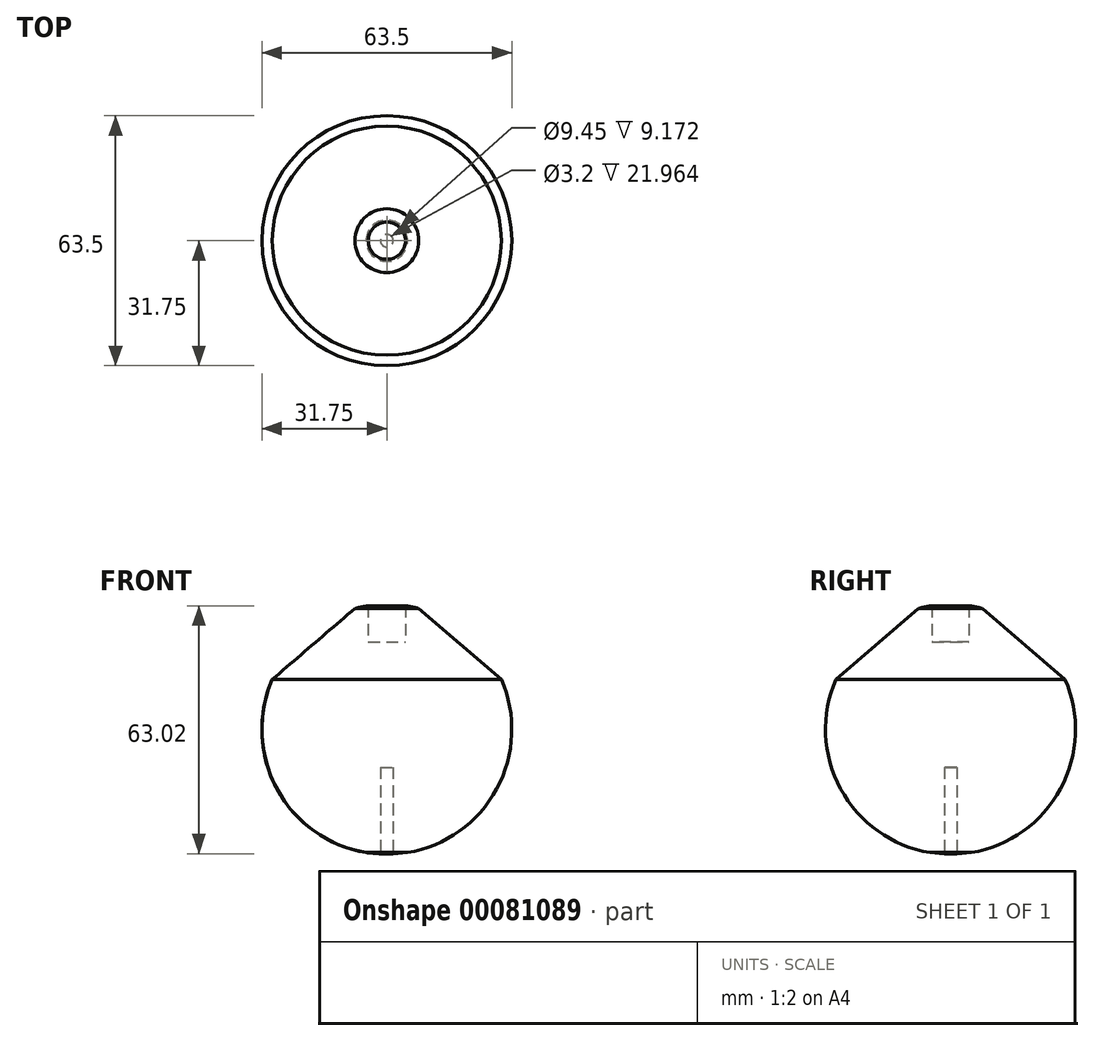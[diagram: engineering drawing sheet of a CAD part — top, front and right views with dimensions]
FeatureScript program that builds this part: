
annotation { "Feature Type Name" : "Feature", "Feature Type Description" : "" }
export const myFeature = defineFeature(function(context is Context, id is Id, definition is map)
    precondition{}
    {
        {
            var Q0;
            Q0=qCreatedBy(makeId("Front.planeOp"),FACE);
            var sketch = newSketch(context, id + "F0", { "sketchPlane" : qUnion([Q0])});
            skArc(sketch, "E0", {"start": v(-22.54, 16.5) * mm, "mid": v(-25.88, -10.52) * mm, "end": v(-4.63, -27.55) * mm});
            skLineSegment(sketch, "E1", {"start": v(0, 0) * mm, "end": v(0, 16.51) * mm});
            skLineSegment(sketch, "E2", {"start": v(0, 16.51) * mm, "end": v(-7.26, 16.51) * mm});
            skLineSegment(sketch, "E3", {"start": v(0, 0) * mm, "end": v(0, -27.94) * mm});
            skLineSegment(sketch, "E4", {"start": v(0, -27.94) * mm, "end": v(0, 35.56) * mm});
            skLineSegment(sketch, "E5", {"start": v(-4.72, 35.56) * mm, "end": v(-4.72, 16.51) * mm});
            skLineSegment(sketch, "E6", {"start": v(0, 35.56) * mm, "end": v(0, 26.03) * mm});
            skLineSegment(sketch, "E7", {"start": v(0, 26.03) * mm, "end": v(-4.72, 26.03) * mm});
            skLineSegment(sketch, "E8.trimOffspring", {"start": v(-7.26, 16.51) * mm, "end": v(22.54, 16.51) * mm});
            skLineSegment(sketch, "E9.trimOffspring", {"start": v(-19.3, 16.51) * mm, "end": v(-22.54, 16.51) * mm});
            skPoint(sketch, "E10", {"position": v(-7.26, -3.67) * mm});
            skPoint(sketch, "E11", {"position": v(-16.16, -5.93) * mm});
            skPoint(sketch, "E12", {"position": v(-24.25, -7.55) * mm});
            skLineSegment(sketch, "E13", {"start": v(-24.25, -7.55) * mm, "end": v(-24.25, -7.55) * mm});
            skPoint(sketch, "E14", {"position": v(-24.43, 6.97) * mm});
            skPoint(sketch, "E15.3.internal.snap0", {"position": v(7.64, 16.51) * mm});
            skLineSegment(sketch, "E16", {"start": v(-1.6, -27.8) * mm, "end": v(-13.82, -26.79) * mm});
            skLineSegment(sketch, "E17", {"start": v(0, -27.94) * mm, "end": v(0, -5.84) * mm});
            skLineSegment(sketch, "E18", {"start": v(0, -5.84) * mm, "end": v(-1.6, -5.84) * mm});
            skLineSegment(sketch, "E19", {"start": v(-1.6, -5.84) * mm, "end": v(-1.6, -27.8) * mm});
            skArc(sketch, "E20.trimOffspring", {"start": v(0, -27.94) * mm, "mid": v(24.92, -12.64) * mm, "end": v(22.54, 16.51) * mm});
            skArc(sketch, "E21.trimOffspring", {"start": v(0, -25.4) * mm, "mid": v(23.07, -10.63) * mm, "end": v(19.3, 16.51) * mm});
            skLineSegment(sketch, "E22", {"start": v(-22.54, 16.5) * mm, "end": v(-8.1, 34.5) * mm});
            skFitSpline(sketch, "E23.trimOffspring", {"points": [v(-24.43, 6.97) * mm, v(-7.26, 12.37) * mm, v(-9.1, 16.51) * mm], "startDerivative": vector(32.41, -14.69) * mm, "endDerivative": vector(-11.55, 14.27) * mm});
            skLineSegment(sketch, "E24", {"start": v(0, -27.94) * mm, "end": v(0, 3.8) * mm});
            skArc(sketch, "E25", {"start": v(-4.72, 35.2) * mm, "mid": v(-6.43, 34.9) * mm, "end": v(-8.1, 34.5) * mm});
            skLineSegment(sketch, "E26", {"start": v(-1.6, -27.8) * mm, "end": v(-1.6, -27.9) * mm});
            skArc(sketch, "E27.trimOffspring", {"start": v(0, -27.94) * mm, "mid": v(31.75, 3.8) * mm, "end": v(0, 35.56) * mm});
            skLineSegment(sketch, "E28", {"start": v(-22.54, 16.5) * mm, "end": v(-29.1, 16.5) * mm});
            skLineSegment(sketch, "E29", {"start": v(-29.1, 16.5) * mm, "end": v(-8.1, 34.5) * mm});
            skArc(sketch, "E30.trimOffspring", {"start": v(-29.1, 16.5) * mm, "mid": v(-27, -12.9) * mm, "end": v(-1.6, -27.9) * mm});
            skSolve(sketch);
        }
        {
            var Q0;
            {var subQ0=sQuery(id+"F0.wireOp",EDGE,"E13");var subQ1=sQuery(id+"F0.wireOp",EDGE,"tVGfZYd6-jjf8-WeDL-8lbz-A1Di6X17U0wS");var subQ2=makeQuery(id+"F0.imprint","INTERSECT",VERTEX,{"disambiguationData":[OD(0.0)],"derivedFrom":[subQ1,subQ0]});Q0=makeQuery(id+"F0.imprint","IMPRINT",FACE,{"disambiguationData":[TD([[makeQuery(id+"F0.imprint","IMPRINT",EDGE,{"disambiguationData":[TD([[subQ2,-1.0]])],"derivedFrom":subQ1}),1.0]])]});}
            var Q1;
            {var subQ0=sQuery(id+"F0.wireOp",EDGE,"tVGfZYd6-jjf8-WeDL-8lbz-A1Di6X17U0wS");var subQ1=sQuery(id+"F0.wireOp",EDGE,"bDiMBlMv-fEZ2-t5qV-gFNT-cdJ1VpS5pjVa");var subQ2=makeQuery(id+"F0.imprint","INTERSECT",VERTEX,{"derivedFrom":[subQ1,subQ0]});Q1=makeQuery(id+"F0.imprint","IMPRINT",FACE,{"disambiguationData":[TD([[makeQuery(id+"F0.imprint","IMPRINT",EDGE,{"disambiguationData":[TD([[subQ2,1.0]])],"derivedFrom":subQ1}),1.0]])]});}
            var Q2;
            {var subQ0=sQuery(id+"F0.wireOp",EDGE,"E7");Q2=makeQuery(id+"F0.imprint","IMPRINT",FACE,{"disambiguationData":[TD([[makeQuery(id+"F0.imprint","IMPRINT",EDGE,{"derivedFrom":subQ0}),1.0]])]});}
            var Q3;
            {var subQ1=sQuery(id+"F0.wireOp",EDGE,"3YQgeERK-oHEF-YljJ-OKs6-JBzS4GsUTOJ7");Q3=makeQuery(id+"F0.imprint","IMPRINT",FACE,{"disambiguationData":[TD([[makeQuery(id+"F0.imprint","IMPRINT",EDGE,{"derivedFrom":subQ1}),1.0]])]});}
            var Q4;
            {var subQ4=sQuery(id+"F0.wireOp",EDGE,"E9.trimOffspring");Q4=makeQuery(id+"F0.imprint","IMPRINT",FACE,{"disambiguationData":[TD([[makeQuery(id+"F0.imprint","IMPRINT",EDGE,{"derivedFrom":subQ4}),1.0]])]});}
            var Q5;
            {var subQ0=sQuery(id+"F0.wireOp",EDGE,"E4");var subQ1=makeQuery(id+"F0.imprint","IMPRINT",VERTEX,{"derivedFrom":subQ0});Q5=makeQuery(id+"F0.imprint","IMPRINT",FACE,{"disambiguationData":[TD([[makeQuery(id+"F0.imprint","IMPRINT",EDGE,{"disambiguationData":[TD([[subQ1,1.0]])],"derivedFrom":subQ0}),1.0]])]});}
            var Q6;
            {var subQ1=sQuery(id+"F0.wireOp",EDGE,"bDiMBlMv-fEZ2-t5qV-gFNT-cdJ1VpS5pjVa");var subQ8=sQuery(id+"F0.wireOp",EDGE,"E5");var subQ9=makeQuery(id+"F0.imprint","INTERSECT",VERTEX,{"derivedFrom":[subQ1,subQ8]});Q6=makeQuery(id+"F0.imprint","IMPRINT",FACE,{"disambiguationData":[TD([[makeQuery(id+"F0.imprint","IMPRINT",EDGE,{"disambiguationData":[TD([[subQ9,1.0]])],"derivedFrom":subQ1}),1.0]])]});}
            var Q7;
            Q7=sQuery(id+"F0.wireOp",EDGE,"E4");
            revolve(context, id + "F1", {"entities" : qUnion([Q0, Q1, Q2, Q3, Q4, Q5, Q6]), "axis" : qUnion([Q7]), "revolveType" : RevolveType.FULL});
        }
        {
            var Q0;
            {var subQ2=sQuery(id+"F0.wireOp",EDGE,"E0");Q0=makeQuery(id+"F0.imprint","IMPRINT",FACE,{"disambiguationData":[TD([[makeQuery(id+"F0.imprint","IMPRINT",EDGE,{"derivedFrom":subQ2}),1.0]])]});}
            var Q1;
            {var subQ0=sQuery(id+"F0.wireOp",EDGE,"E0");Q1=makeQuery(id+"F0.imprint","IMPRINT",FACE,{"disambiguationData":[TD([[makeQuery(id+"F0.imprint","IMPRINT",EDGE,{"derivedFrom":subQ0}),-1.0]])]});}
            var Q2;
            Q2=makeQuery(id+"F0.imprint","IMPRINT",FACE,{"disambiguationData":[TD([[makeQuery(id+"F0.imprint","IMPRINT",EDGE,{"derivedFrom":sQuery(id+"F0.wireOp",EDGE,"E22")}),1.0]])]});
            var Q3;
            Q3=sQuery(id+"F0.wireOp",EDGE,"E24");
            revolve(context, id + "F2", {"operationType" : NewBodyOperationType.ADD, "entities" : qUnion([Q0, Q1, Q2]), "axis" : qUnion([Q3]), "revolveType" : RevolveType.FULL});
        }
    });
